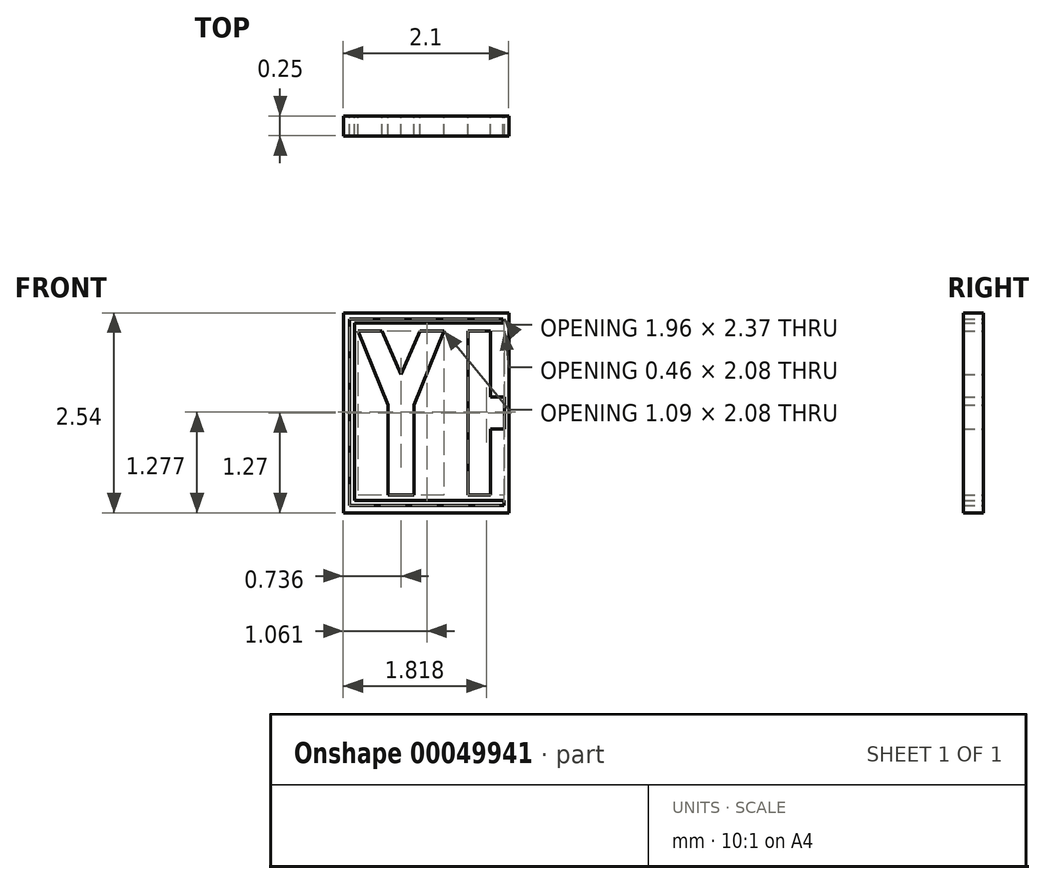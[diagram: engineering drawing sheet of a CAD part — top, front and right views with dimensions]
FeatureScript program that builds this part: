
annotation { "Feature Type Name" : "Feature", "Feature Type Description" : "" }
export const myFeature = defineFeature(function(context is Context, id is Id, definition is map)
    precondition{}
    {
        {
            var Q0;
            Q0=qCreatedBy(makeId("Front.planeOp"),FACE);
            var sketch = newSketch(context, id + "F0", { "sketchPlane" : qUnion([Q0])});
            skLineSegment(sketch, "E0", {"start": v(2.54, 0) * mm, "end": v(2.54, 2.54) * mm});
            skLineSegment(sketch, "E1", {"start": v(2.54, 2.54) * mm, "end": v(0, 2.54) * mm});
            skLineSegment(sketch, "E2", {"start": v(2.31, 2.31) * mm, "end": v(2.03, 2.31) * mm});
            skLineSegment(sketch, "E3", {"start": v(2.03, 2.31) * mm, "end": v(2.03, 0.23) * mm});
            skLineSegment(sketch, "E4", {"start": v(2.31, 0.23) * mm, "end": v(2.03, 0.23) * mm});
            skLineSegment(sketch, "E5", {"start": v(2.31, 2.31) * mm, "end": v(2.31, 1.47) * mm});
            skLineSegment(sketch, "E6", {"start": v(2.31, 0.23) * mm, "end": v(2.31, 1.07) * mm});
            skLineSegment(sketch, "E7", {"start": v(1.01, 0.23) * mm, "end": v(1.01, 1.37) * mm});
            skLineSegment(sketch, "E8", {"start": v(1.34, 0.23) * mm, "end": v(1.34, 1.37) * mm});
            skLineSegment(sketch, "E9", {"start": v(1.72, 2.31) * mm, "end": v(1.42, 2.31) * mm});
            skLineSegment(sketch, "E10", {"start": v(0.63, 2.31) * mm, "end": v(0.93, 2.31) * mm});
            skLineSegment(sketch, "E11", {"start": v(0.63, 2.31) * mm, "end": v(1.01, 1.37) * mm});
            skLineSegment(sketch, "E12", {"start": v(1.72, 2.31) * mm, "end": v(1.34, 1.37) * mm});
            skLineSegment(sketch, "E13", {"start": v(0.93, 2.31) * mm, "end": v(1.18, 1.75) * mm});
            skLineSegment(sketch, "E14", {"start": v(1.42, 2.31) * mm, "end": v(1.18, 1.75) * mm});
            skLineSegment(sketch, "E15", {"start": v(1.01, 0.23) * mm, "end": v(1.34, 0.23) * mm});
            skLineSegment(sketch, "E16", {"start": v(0.14, 1.49) * mm, "end": v(0.32, 1.49) * mm});
            skLineSegment(sketch, "E17", {"start": v(0.16, 1.05) * mm, "end": v(0.32, 1.05) * mm});
            skLineSegment(sketch, "E18", {"start": v(0.16, 0.8) * mm, "end": v(0.32, 0.8) * mm});
            skLineSegment(sketch, "E19", {"start": v(0.14, 1.74) * mm, "end": v(0.32, 1.74) * mm});
            skLineSegment(sketch, "E20", {"start": v(0.32, 1.49) * mm, "end": v(0.32, 1.05) * mm});
            skLineSegment(sketch, "E21", {"start": v(0.32, 0.8) * mm, "end": v(0.32, 0.23) * mm});
            skLineSegment(sketch, "E22", {"start": v(0.32, 2.31) * mm, "end": v(0.32, 1.74) * mm});
            skLineSegment(sketch, "E23", {"start": v(2.49, 1.47) * mm, "end": v(2.49, 1.07) * mm});
            skLineSegment(sketch, "E24", {"start": v(2.31, 1.47) * mm, "end": v(2.49, 1.47) * mm});
            skLineSegment(sketch, "E25", {"start": v(2.49, 1.07) * mm, "end": v(2.31, 1.07) * mm});
            skLineSegment(sketch, "E26", {"start": v(0, 2.5) * mm, "end": v(0.05, 2.5) * mm});
            skLineSegment(sketch, "E27", {"start": v(0.16, 0.8) * mm, "end": v(0.05, 0.8) * mm});
            skLineSegment(sketch, "E28", {"start": v(0.32, 0.23) * mm, "end": v(0.05, 0.23) * mm});
            skLineSegment(sketch, "E29", {"start": v(0.16, 1.05) * mm, "end": v(0.05, 1.05) * mm});
            skLineSegment(sketch, "E30", {"start": v(0.14, 1.49) * mm, "end": v(0.05, 1.49) * mm});
            skLineSegment(sketch, "E31", {"start": v(0.14, 1.74) * mm, "end": v(0.05, 1.74) * mm});
            skLineSegment(sketch, "E32", {"start": v(0.32, 2.31) * mm, "end": v(0.05, 2.31) * mm});
            skLineSegment(sketch, "E33", {"start": v(0.05, 2.31) * mm, "end": v(0.05, 1.74) * mm});
            skLineSegment(sketch, "E34", {"start": v(0.05, 1.49) * mm, "end": v(0.05, 1.05) * mm});
            skLineSegment(sketch, "E35", {"start": v(0.05, 0.8) * mm, "end": v(0.05, 0.23) * mm});
            skLineSegment(sketch, "E36", {"start": v(0.44, 2.54) * mm, "end": v(0.44, 0) * mm});
            skLineSegment(sketch, "E37", {"start": v(0.44, 0) * mm, "end": v(2.54, 0) * mm});
            skLineSegment(sketch, "E38", {"start": v(2.47, 2.54) * mm, "end": v(2.47, 2.46) * mm});
            skLineSegment(sketch, "E39", {"start": v(2.47, 2.46) * mm, "end": v(2.54, 2.46) * mm});
            skLineSegment(sketch, "E40", {"start": v(2.47, 2.46) * mm, "end": v(0.52, 2.46) * mm});
            skLineSegment(sketch, "E41", {"start": v(0.52, 2.46) * mm, "end": v(0.52, 0.09) * mm});
            skLineSegment(sketch, "E42", {"start": v(0.52, 0.09) * mm, "end": v(0.58, 0.09) * mm});
            skLineSegment(sketch, "E43", {"start": v(0.58, 0.09) * mm, "end": v(0.58, 2.41) * mm});
            skLineSegment(sketch, "E44", {"start": v(0.58, 2.41) * mm, "end": v(2.47, 2.41) * mm});
            skLineSegment(sketch, "E45", {"start": v(2.47, 2.41) * mm, "end": v(2.47, 2.46) * mm});
            skLineSegment(sketch, "E46", {"start": v(0.58, 0.09) * mm, "end": v(2.48, 0.09) * mm});
            skLineSegment(sketch, "E47", {"start": v(2.48, 0.09) * mm, "end": v(2.48, 0.16) * mm});
            skLineSegment(sketch, "E48", {"start": v(2.48, 0.16) * mm, "end": v(0.58, 0.16) * mm});
            skSolve(sketch);
        }
        {
            var Q0;
            {var subQ4=sQuery(id+"F0.wireOp",EDGE,"E38");Q0=makeQuery(id+"F0.imprint","IMPRINT",FACE,{"disambiguationData":[TD([[makeQuery(id+"F0.imprint","IMPRINT",EDGE,{"derivedFrom":subQ4}),1.0]])]});}
            var Q1;
            Q1=makeQuery(id+"F0.imprint","IMPRINT",FACE,{"disambiguationData":[TD([[makeQuery(id+"F0.imprint","IMPRINT",EDGE,{"derivedFrom":sQuery(id+"F0.wireOp",EDGE,"E2")}),-1.0]])]});
            extrude(context, id + "F1", {"entities" : qUnion([Q0, Q1]), "depth" : 0.25 * mm});
        }
    });
